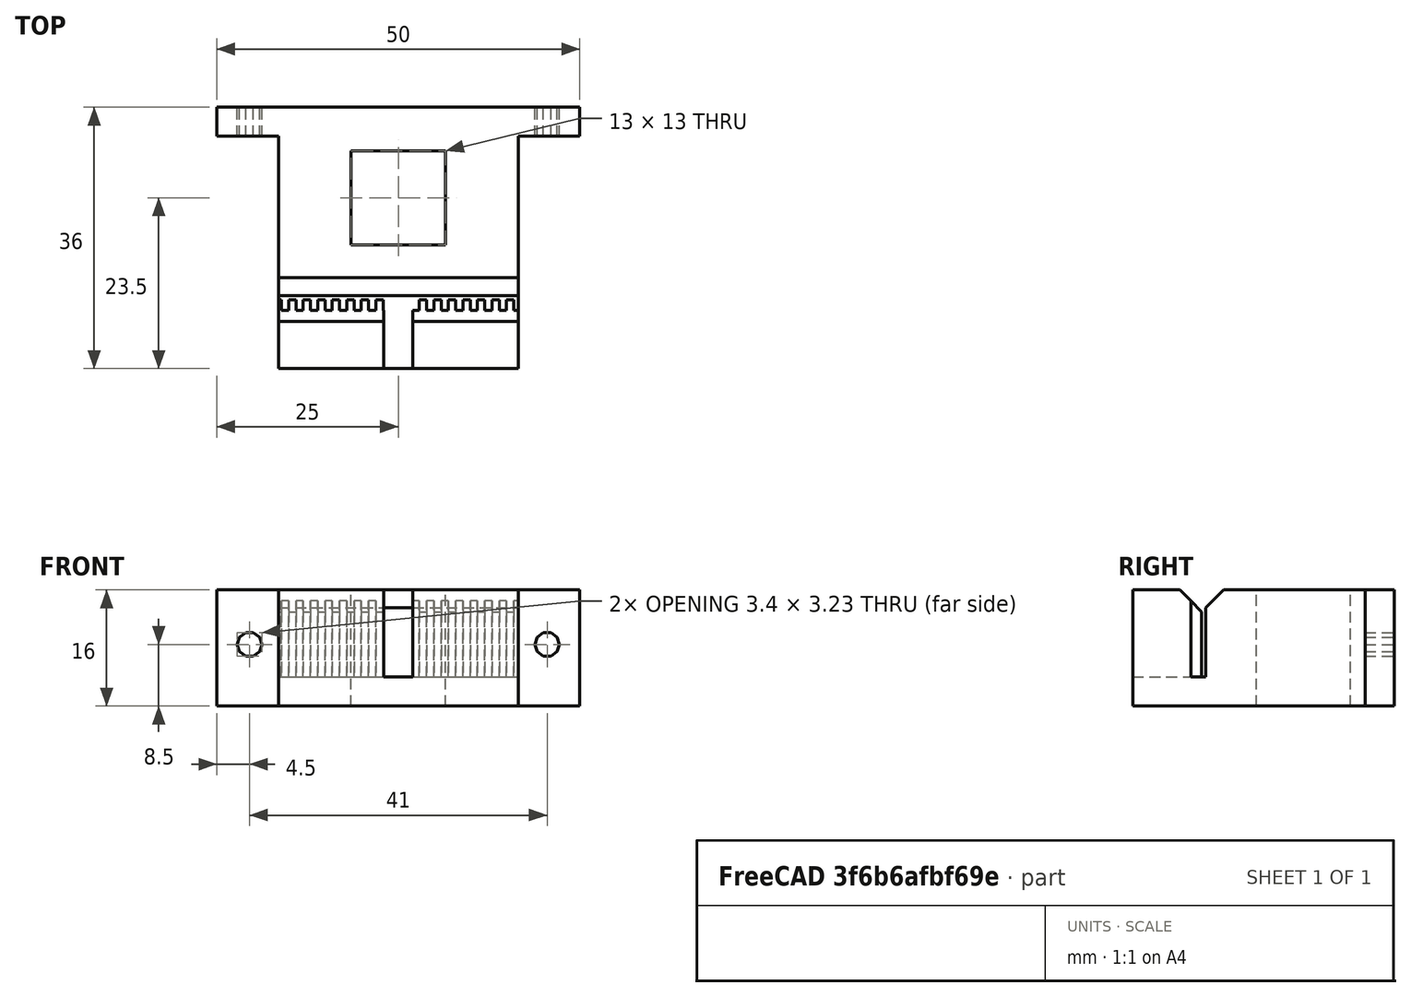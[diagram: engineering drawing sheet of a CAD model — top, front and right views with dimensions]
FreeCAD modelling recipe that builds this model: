
FCSTD DOCUMENT  (FreeCAD 0.19R)
Label: y-belt-holder
License: All rights reserved
LicenseURL: http://en.wikipedia.org/wiki/All_rights_reserved
objects: Part::Box×31, Part::MultiFuse×3, Part::Prism×2, Part::Fuse×2, Part::Cut×1
note: 39 computed .brp shape members not serialized (recipe doc carries the construction recipe); baked Part::Feature solids carry a one-line shape summary decoded from their .brp

FEATURE [Part::Box] cube
  AttacherType = Attacher::AttachEngine3D
  Height = 16
  Length = 33
  Placement = pos=(-41.5,0,-1) rot=(0,0,1;0rad)
  Width = 15
FEATURE [Part::Box] cube001
  AttacherType = Attacher::AttachEngine3D
  Height = 16
  Length = 33
  Placement = pos=(-41.5,11,-1) rot=(0,0,1;0rad)
  Width = 25
FEATURE [Part::Box] cube002
  AttacherType = Attacher::AttachEngine3D
  Height = 16
  Length = 50
  Placement = pos=(-50,32,-1) rot=(0,0,1;0rad)
  Width = 4
FEATURE [Part::MultiFuse] Group
  Shapes = -> [cube,cube001,cube002]
FEATURE [Part::Box] cube003
  AttacherType = Attacher::AttachEngine3D
  Height = 15
  Length = 67
  Placement = pos=(-66,9.5,3) rot=(0,0,1;0rad)
  Width = 0.55
FEATURE [Part::Box] cube004
  AttacherType = Attacher::AttachEngine3D
  Height = 15
  Length = 67
  Placement = pos=(-66,9.5,12) rot=(1,0,0;0.785398rad)
  Width = 15
FEATURE [Part::Box] cube005 .. cube028  x24 (patterned run collapsed; names and placements below)
  AttacherType = Attacher::AttachEngine3D
  Height = 15
  Length = 1
  Width = 1.7
  placements: 24 in arithmetic series — first pos=(-1.1,8,3) rot=(0,0,1;0rad), step (-2,0,0), last pos=(-47.1,8,3) rot=(0,0,1;0rad)
FEATURE [Part::MultiFuse] Group001
  Shapes = -> [cube005,cube006,cube007,cube008,cube009,cube010,cube011,cube012,cube013,cube014,cube015,cube016,cube017,cube018,cube019,cube020,cube021,cube022,cube023,cube024,cube025,cube026,cube027,cube028]
FEATURE [Part::Box] cube029
  AttacherType = Attacher::AttachEngine3D
  Height = 15
  Length = 4
  Placement = pos=(-27,-1,3) rot=(0,0,1;0rad)
  Width = 11
FEATURE [Part::Box] cube030
  AttacherType = Attacher::AttachEngine3D
  Height = 20
  Length = 13
  Placement = pos=(-31.5,17,-2) rot=(0,0,1;0rad)
  Width = 13
FEATURE [Part::MultiFuse] Group002
  Shapes = -> [cube003,cube004,Group001,cube029,cube030]
FEATURE [Part::Prism] prism
  AttacherType = Attacher::AttachEngine3D
  Circumradius = 1.7
  FirstAngle = 0
  Height = 50
  Placement = pos=(-4.5,0.1,7.5) rot=(-1,0,0;1.5708rad)
  Polygon = 10
  SecondAngle = 0
FEATURE [Part::Prism] prism001
  AttacherType = Attacher::AttachEngine3D
  Circumradius = 1.7
  FirstAngle = 0
  Height = 50
  Placement = pos=(-45.5,0.1,7.5) rot=(-1,0,0;1.5708rad)
  Polygon = 10
  SecondAngle = 0
FEATURE [Part::Fuse] Group003
  Base = -> prism
  Tool = -> prism001
FEATURE [Part::Fuse] union
  Base = -> Group002
  Tool = -> Group003
FEATURE [Part::Cut] difference
  Base = -> Group
  Refine = true
  Tool = -> union
